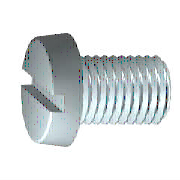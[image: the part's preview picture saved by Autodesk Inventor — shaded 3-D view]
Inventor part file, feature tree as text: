
AUTODESK INVENTOR PART (.ipt)
format: ipt  version: 2023.2 (Build 272271030, 271C)  size: 187,392 bytes
history: native  units: mm (DEFAULTED — no unit token found)
features: sketch x2, extrude x1, plane x1
ambient origin geometry x7: Origin, YZ Plane, XZ Plane, X Axis, Y Axis, Z Axis, Center Point
bodies: Solid1 (feature_tree), Body (feature_tree)
feature tree (4):
  sketch  "Sketch2"  dims[d2=0.49086mm d3=3.3mm d4=5.0mm d5=4.566987mm d8=90.0deg d7=0.0mm d9=8.5mm d10=0.872665mm d11=1.2mm d12=8.5mm d14=0.2mm d15=4.4mm d16=0.0mm d17=0.433015mm d18=0.49086mm d19=1.3mm d20=0.0mm d36=45.0deg d37=0.0mm d39=0.0mm]
  extrude  "Slot"  Depth=4.4mm
  plane  "Work Plane1"
  sketch  "Sketch1"  dims[d0=6.0mm d1=4.4mm]
